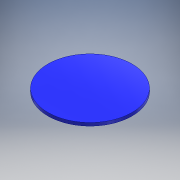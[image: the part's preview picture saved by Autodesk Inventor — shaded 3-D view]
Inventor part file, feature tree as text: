
AUTODESK INVENTOR PART (.ipt)
format: ipt  version: 2018.3 (Build 223284000, 284)  size: 92,672 bytes
history: native  units: mm
features: extrude x1, sketch x1
ambient origin geometry x8: Origin, YZ Plane, XZ Plane, XY Plane, X Axis, Y Axis, Z Axis, Center Point
bodies: Solid1 (feature_tree)
feature tree (2):
  extrude  "Extrusion1"  Depth=1.0mm TaperAngle=0.0deg
  sketch  "Sketch1"  dims[d0=27.0mm d1=1.0mm d2=0.0mm]
